# Revit family: xLIFE-xx-xx-SM_V1.0_Non-Hosted_R16
name_source: partatom
category: Lighting Fixtures
revit_build: Autodesk Revit 2016 (Build: 20151007_0715(x64)
units: mm (PartAtom-declared; Revit-internal decimal feet)

## family parameters
Always vertical = Yes
Cut with Voids When Loaded = No
Light Source = Yes
OmniClass Number = 23.80.70.00
OmniClass Title = Lighting
Part Type = Normal
Room Calculation Point = No
Round Connector Dimension = Use Diameter
Shared = No
Work Plane-Based = No

## types (27) — shared parameters
Charging Method = Intelligent Current Limited Constant Voltage
Color Filter = 16777215
Construction = Polycarbonate Enclosure
Dimensions (Lx W x H) = 242mm x 125mm x 48mm
Dimming Lamp Color Temperature Shift = <None>
Emit Shape Visible in Rendering = No
Emit from Rectangle Length = 1219 mm
Emit from Rectangle Width = 610 mm
IP Rating = IP20
Manufacturer = Clevertronics
Mounting = Surface Mount
Operating Mode = Non-maintained
Operating Temperature = 1˚C to 40˚C
Operating Voltage = 240V AC; 50Hz
Tilt Angle = 90.00°

## per-type parameters (varying)
| type | AS2293 Classification | Battery | Battery Type | Lamp | MIC Number | Photometric Web File | Power Consumption | Power Consumption (Standby) | Product Description | Replacement Battery | Replacement Driver | Testing Node | Testing System | Weight |
| ELIFE-X-LI-SM | C0=D40 C90=D40 | 3.2V 3200mAh | Lithium Iron Phosphate | 1 x High intensity LED | AUD03310010001 | ll22526_ELIFE-X-LI-SM(AUD03310010001,AS2293.3,Classification).ies | 1.3W (Max) | 0.4 W | Economy Lithium Lifelight, Surface Mounted Emergency Light | 1560160 BATT:EcoLith 3.2V 3.0Ah 170mm lead,NoBKT | 8002986 PCA: ELIFE-X-SMS-LI CT10614-L2 |  | N/A - Manual test switch | 0.6kg |
| LLIFE-SM-ZW | C0=D40 C90=D40 | 3.3V 2500mAh | Lithium Nanophosphate | 1 x High intensity LED | AUD01110050001 | LL22405 - CLIFE-SM-ZW (AUD02110010001, AS2293.3, 2-hr Photometry).ies | 2.7 Watts (Max) | 1.3 Watts | L10 Optimum Lifelight, High Performance, Surface Mounted Emergency Light | 1530071 BATTERY:L10 3.3V 2.5AH 200mm ld, no Brkt |  | 8001450 PCA:Powerline Node ZW, #CT10310-A6 | Zoneworks Computerised Testing | 0.6kg |
| LLIFE-SM-DALI | C0=D40 C90=D40 | 3.3V 2500mAh | Lithium Nanophosphate | 1 x High intensity LED | AUD01210070002 | LL22405 - CLIFE-SM-ZW (AUD02110010001, AS2293.3, 2-hr Photometry).ies | 2.7 Watts | 0.4 Watts | L10 Optimum Lifelight, High Performance, Surface Mounted Emergency Ligh | 1530071 BATTERY:L10 3.3V 2.5AH 200mm ld, no Brkt |  | 8003060 PCA: New DALI #CT10629-Ax | DALI Registered | 0.6kg |
| LLIFE-SM | C0=D40 C90=D40 | 3.3V 2500mAh | Lithium Nanophosphate | 1 x High intensity LED | AUD01310060001 | LL22405 - CLIFE-SM-ZW (AUD02110010001, AS2293.3, 2-hr Photometry).ies | 3.0 Watts | 1.3 Watts | L10 Optimum Lifelight, High Performance, Surface Mounted Emergency Light, Enabled
with Clevertest Plus | 1530071 BATTERY:L10 3.3V 2.5AH 200mm ld, no Brkt |  | 8002938 PCA: LLIFE CT10260-L5 1C550 CTP AU Vert Connectors | Clevertest Plus Enabled (Not activated by default) | 0.6kg |
| LLIFE-SM-BLK | C0=D40 C90=D40 | 3.3V 2.5AH | Lithium Iron Phosphate (LiFePO4), | 1 x LED | AUD01310070001 | LL22405 - CLIFE-SM-ZW (AUD02110010001, AS2293.3, 2-hr Photometry).ies | 4.2 Watts | 1.0 Watts | L10 Optimum LifeLight, High Performance, Recessed Emergency Light, Black, with Clevertest
L10 Optimum LifeLight, High Performance, Recessed Emergency Light, Black, with Clevertest
Plus Enabled


with Clevertest Plus | 1530071 BATTERY:L10 3.3V 2.5AH 200mm ld, no Brkt |  | 8002938 PCA: LLIFE CT10260-L5 1C550 CTP AU Vert Connectors | Clevertest Plus Enabled (Not activated by default) | 0.7kg |
| LLIFE-SM-HV | C0=D40 C90=D40 | 3.3V 2.5AH | Lithium Nanophosphate, | 1 x High intensity LED | AUD01810030001 | LL22405 - CLIFE-SM-ZW (AUD02110010001, AS2293.3, 2-hr Photometry).ies | 2.7 Watts | 0.4 Watts | L10 Optimum Lifelight, High Performance, Surface Mounted Emergency Light
L10 Optimum LifeLight, High Performance, Recessed Emergency Light, Black, with Clevertest
Plus Enabled


with Clevertest Plus | 1530071 BATTERY:L10 3.3V 2.5AH 200mm ld, no Brkt |  | 8003190 PCA: RF Node CT10678-Ax internal antenna | Zoneworks XT HIVE (RF) | 0.6kg |
| LLIFE-SM-HV-BLK | C0=D40 C90=D40 | 3.3V 2.5AH | Lithium Nanophosphate, | 1 x High intensity LED | AUD02810110001 | LL22405 - CLIFE-SM-ZW (AUD02110010001, AS2293.3, 2-hr Photometry).ies | 2.7 Watts | 1.3 Watts | L10 Optimum Lifelight, High Performance, Surface Mounted Emergency Light, Black
L10 Optimum LifeLight, High Performance, Recessed Emergency Light, Black, with Clevertest
Plus Enabled


with Clevertest Plus | 1530071 BATTERY:L10 3.3V 2.5AH 200mm ld, no Brkt |  | 8003190 PCA: RF Node CT10678-Ax internal antenna | Zoneworks XT HIVE (RF) | 0.6kg |
| CLIFE-SM-ZW | C0=D40 C90=D40 | 3.2V 3200mAh | Lithium Iron Phosphate | 1 x LED | AUD02110010001 | LL22405 - CLIFE-SM-ZW (AUD02110010001, AS2293.3, 2-hr Photometry).ies | 3.9 Watts | 1.0 W | LP Premium Lifelight, High Performance, Surface Mounted Emergency Light | 1550030 BATT:LP 3.2V 3200mAh 260mm lead,noBRKT |  | 8001450 PCA:Powerline Node ZW, #CT10310-A6 | Zoneworks computerised testing | 0.7kg |
| CLIFE-SM-ZW-BLK | C0=D40 C90=D40 | 3.2V 3200mAh | Lithium Iron Phosphate | 1 x LED | AUD02110060001 | LL22405 - CLIFE-SM-ZW (AUD02110010001, AS2293.3, 2-hr Photometry).ies | 3.9 Watts | 1.0 W | LP Premium Lifelight, High Performance, Surface Mounted Emergency Light, Black | 1550030 BATT:LP 3.2V 3200mAh 260mm lead,noBRKT |  | 8001450 PCA:Powerline Node ZW, #CT10310-A6 | Zoneworks computerised testing | 0.7kg |
| CLIFE-SM-DALI | C0=D40 C90=D40 | 3.2V 3200mAh | Lithium Iron Phosphate | 1 x LED | AUD02210200002 | LL22405 - CLIFE-SM-ZW (AUD02110010001, AS2293.3, 2-hr Photometry).ies | 3.9 Watts | 1.0 W | LP Premium Lifelight, High Performance, Surface Mounted Emergency Light | 1550030 BATT:LP 3.2V 3200mAh 260mm lead,noBRKT |  | 8003060 PCA: DALI Node #CT10629-Ax | DALI Registered | 0.7kg |
| CLIFE-SM | C0=D40 C90=D40 | 3.2V 3200mAh | Lithium Iron Phosphate | 1 x LED | AUD02310030001 | LL22405 - CLIFE-SM-ZW (AUD02110010001, AS2293.3, 2-hr Photometry).ies | 3.9 Watts | 1.0 W | LP Premium Lifelight, High Performance, Surface Mounted Emergency Light, Enabled with
Clevertest Plus | 1550030 BATT:LP 3.2V 3200mAh 260mm lead,noBRKT |  | 8002934 PCA: CLIFE CT10260-L5 1C650 CTP AU Vert Connectors | Clevertest Plus Enabled (Not activated by default) | 0.7kg |
| CLIFE-SM-4HR | C0=D40 C90=D40 | 3.2V 6400mAh | Lithium Iron Phosphate | 1 x High intensity LED | AUD02310080001 | LL22405 - CLIFE-SM-ZW (AUD02110010001, AS2293.3, 2-hr Photometry).ies | 3.9 Watts | 1.0 W | LP Premium Lifelight, High Performance, Surface Mounted Emergency Light with 4 Hour
Emergency Operation
Clevertest Plus | 1550231 BATT:LP 3.2V 6400mAh.200mm lead, No Brkt |  | 8002934 PCA: CLIFE CT10260-L5 1C650 CTP AU Vert Connectors | Manual (see datasheet) | 0.7kg |
| CLIFE-SM-HV | C0=D40 C90=D40 | 3.2V 3200mAh | Lithium Iron Phosphate | 1 x High intensity LED | AUD02810080001 | LL22405 - CLIFE-SM-ZW (AUD02110010001, AS2293.3, 2-hr Photometry).ies | 3.9 Watts | 1.0 W | LP Premium Lifelight, High Performance, Surface Mounted Emergency Light | 1550030 BATT:LP 3.2V 3200mAh 260mm lead,noBRKT. |  | 8003190 PCA: RF Node CT10678-Ax Int Antenna | Zoneworks XT HIVE (RF) | 0.7kg |
| CLIFE-SM-BLK | C0=D40 C90=D40 | 3.2V 3200mAh | Lithium Iron Phosphate | 1 x High intensity LED | AUD02810090001 | LL22405 - CLIFE-SM-ZW (AUD02110010001, AS2293.3, 2-hr Photometry).ies | 3.9 Watts | 1.0 W | LP Premium Lifelight, High Performance, Surface Mounted Emergency Light, Black,
Enabled with Clevertest Plus | 1550030 BATT:LP 3.2V 3200mAh 260mm lead,noBRKT. |  | 8002934 PCA: CLIFE CT10260-L5 1C650 CTP AU Vert Connectors | Clevertest Plus Enabled (Not activated by default) | 0.7kg |
| CLIFE-SM-HV-BLK | C0=D40 C90=D40 | 3.2V 3200mAh | Lithium Iron Phosphate | 1 x High intensity LED | AUD02810100001 | LL22405 - CLIFE-SM-ZW (AUD02110010001, AS2293.3, 2-hr Photometry).ies | 3.9 Watts | 1.0 W | LP Premium Lifelight, High Performance, Surface Mounted Emergency Light, Black
Enabled with Clevertest Plus | 1550030 BATT:LP 3.2V 3200mAh 260mm lead,noBRKT. |  | 8003190 PCA: RF Node CT10678-Ax Int Antenna | Zoneworks XT HIVE (RF) | 0.7kg |
| LLIFE-PRO-SM-DALI | C0=D80 C90=D80 | 3.3V 5000mAh | Lithium Nanophosphate | Dual LED | AUT01210570002 | ll22440(AS2293.3_Photometry).ies | 4.7 Watts | 0.4W | L10 Optimum Lifelight PRO, High Performance, Surface Mounted Emergency Light
Enabled with Clevertest Plus | 1530231 BATTERY:L10 3.3V 5AH. 200mm lead.no Brkt |  | 8003060 PCA: New DALI #CT10629-Ax | DALI Registered | 0.7kg |
| LLIFE-PRO-SM | C0=D80 C90=D80 | 3.3V 5000mAh | Lithium Nanophosphate | Dual LED | AUT01310080001 | ll22440(AS2293.3_Photometry).ies | 4.7 Watts | 0.4W | L10 Optimum Lifelight PRO, High Performance, Surface Mounted Emergency Light,
Enabled with Clevertest Plus
Enabled with Clevertest Plus | 1530231 BATTERY:L10 3.3V 5AH. 200mm lead.no Brkt |  | 8002924 PCA: xLIFEPro SM #CT10142-L9 2C250/550 CTP AU | Clevertest Plus Enabled (Not activated by default) | 0.7kg |
| LLIFE-PRO-SM-BLK | C0=D80 C90=D80 | 3.3V 5000mAh | Lithium Nanophosphate | Dual LED | AUT01310110001 | ll22440(AS2293.3_Photometry).ies | 4.7 Watts | 0.4W | L10 Optimum Lifelight PRO, High Performance, Surface Mounted Emergency Light,
Enabled with Clevertest Plus, Black
Enabled with Clevertest Plus
Enabled with Clevertest Plus | 1530231 BATTERY:L10 3.3V 5AH. 200mm lead.no Brkt |  | 8002924 PCA: xLIFEPro SM #CT10142-L9 2C250/550 CTP AU | Clevertest Plus Enabled (Not activated by default) | 0.7kg |
| LLIFE-PRO-SM-HV | C0=D80 C90=D80 | 3.3V 5000mAh | Lithium Nanophosphate | Dual LED | AUT01810030001 | ll22440(AS2293.3_Photometry).ies | 4.7 Watts | 0.4W | L10 Optimum Lifelight PRO, High Performance, Surface Mounted Emergency Light
Enabled with Clevertest Plus, Black
Enabled with Clevertest Plus
Enabled with Clevertest Plus | 1530231 BATTERY:L10 3.3V 5AH. 200mm lead.no Brkt |  | 8003191 PCA: RF Node CT10678-A9 Int Antenna LLPro | Zoneworks XT Hive (RF) | 0.7kg |
| LLIFE-PRO-SM-HV-BLK | C0=D80 C90=D80 | 3.3V 5000mAh | Lithium Nanophosphate | Dual LED | AUT02810070001 | ll22440(AS2293.3_Photometry).ies | 4.7 Watts | 0.4W | L10 Optimum Lifelight PRO, High Performance, Surface Mounted Emergency Light, Black
Enabled with Clevertest Plus, Black
Enabled with Clevertest Plus
Enabled with Clevertest Plus | 1530231 BATTERY:L10 3.3V 5AH. 200mm lead.no Brkt |  | 8003191 PCA: RF Node CT10678-A9 Int Antenna LLPro | Zoneworks XT Hive (RF) | 0.7kg |
| CLIFE-PRO-SM-ZW | C0=D80 C90=D80 | 3.2V 6400mAh | Lithium Iron Phosphate | Dual LED | AUT02110060001 | ll22440(AS2293.3_Photometry).ies | 2.7W Watts | 0.4W | LP Premium Lifelight PRO, High Performance, Surface Mounted Emergency Light
Enabled with Clevertest Plus, Black
Enabled with Clevertest Plus
Enabled with Clevertest Plus | 1550231 BATT:LP 3.2V 6400mAh.200mm lead, No Brkt |  | 8001450 PCA:Powerline Node ZW, #CT10310-A6 | Zoneworks Computerised Testing | 0.7kg |
| CLIFE-PRO-SM-ZW-BLK | C0=D80 C90=D80 | 3.2V 6400mAh | Lithium Iron Phosphate | Dual LED | AUT02110130001 | ll22440(AS2293.3_Photometry).ies | 2.7W Watts | 0.4W | LP Premium Lifelight PRO, High Performance, Surface Mounted Emergency Light
Enabled with Clevertest Plus, Black
Enabled with Clevertest Plus
LP Premium Lifelight PRO, High Performance, Surface Mounted Emergency Light, Black | 1550231 BATT:LP 3.2V 6400mAh.200mm lead, No Brkt |  | 8001450 PCA:Powerline Node ZW, #CT10310-A6 | Zoneworks Computerised Testing | 0.7kg |
| CLIFE-PRO-SM-DALI | C0=D80 C90=D80 | 3.2V 6400mAh | Lithium Iron Phosphate | Dual LED | AUT02210330002 | ll22440(AS2293.3_Photometry).ies | 2.7W Watts | 0.4W | LP Premium Lifelight PRO, High Performance, Surface Mounted Emergency Light
Enabled with Clevertest Plus, Black
Enabled with Clevertest Plus
LP Premium Lifelight PRO, High Performance, Surface Mounted Emergency Light, Black | 1550231 BATT:LP 3.2V 6400mAh.200mm lead, No Brkt |  | 8003060 PCA: New DALI #CT10629-Ax | DALI Registered | 0.7kg |
| CLIFE-PRO-SM | C0=D80 C90=D80 | 3.2V 6400mAh | Lithium Iron Phosphate | Dual LED | AUT02310110001 | ll22440(AS2293.3_Photometry).ies | 4.7W | 0.4W | LP Premium Lifelight PRO, High Performance, Surface Mounted Emergency Light,
Enabled with Clevertest Plus
Enabled with Clevertest Plus, Black
Enabled with Clevertest Plus
LP Premium Lifelight PRO, High Performance, Surface Mounted Emergency Light, Black | 1550231 BATT:LP 3.2V 6400mAh.200mm lead, No Brkt |  | 8002924 PCA: xLIFEPro SM #CT10142-L9 2C250/550 CTP AU | Clevertest Plus Enabled (Not activated by default) | 0.7kg |
| CLIFE-PRO-SM-BLK | C0=D80 C90=D80 | 3.2V 6400mAh | Lithium Iron Phosphate | Dual LED | AUT02310170001 | ll22440(AS2293.3_Photometry).ies | 2.7W Watts | 0.4W | LP Premium Lifelight PRO, High Performance, Surface Mounted Emergency Light,
Enabled with Clevertest Plus, Black
Enabled with Clevertest Plus, Black
Enabled with Clevertest Plus
LP Premium Lifelight PRO, High Performance, Surface Mounted Emergency Light, Black | 1550231 BATT:LP 3.2V 6400mAh.200mm lead, No Brkt |  | 8002924 PCA: xLIFEPro SM #CT10142-L9 2C250/550 CTP AU | Clevertest Plus Enabled (Not activated by default) | 0.7kg |
| CLIFE-PRO-SM-HV | C0=D80 C90=D80 | 3.2V 6400mAh | Lithium Iron Phosphate | Dual LED | AUT02810050001 | ll22440(AS2293.3_Photometry).ies | 2.7W Watts | 0.4W | LP Premium Lifelight PRO, High Performance, Surface Mounted Emergency Light
Enabled with Clevertest Plus, Black
Enabled with Clevertest Plus, Black
Enabled with Clevertest Plus
LP Premium Lifelight PRO, High Performance, Surface Mounted Emergency Light, Black | 1550231 BATT:LP 3.2V 6400mAh.200mm lead, No Brkt |  | 8003191 PCA: RF Node CT10678-A9 Int Antenna LLPro | Zoneworks XT HIVE (RF) | 0.7kg |
| CLIFE-PRO-SM-HV-BLK | C0=D80 C90=D80 | 3.2V 6400mAh | Lithium Iron Phosphate | Dual LED | AUT02810060001 | ll22440(AS2293.3_Photometry).ies | 2.7W Watts | 0.4W | LP Premium Lifelight PRO, High Performance, Surface Mounted Emergency Light,
Black
Enabled with Clevertest Plus, Black
Enabled with Clevertest Plus, Black
Enabled with Clevertest Plus
LP Premium Lifelight PRO, High Performance, Surface Mounted Emergency Light, Black | 1550231 BATT:LP 3.2V 6400mAh.200mm lead, No Brkt |  | 8003191 PCA: RF Node CT10678-A9 Int Antenna LLPro | Zoneworks XT HIVE (RF) | 0.7kg |

note: column(s) folded — value = type name in every type: Model

## geometry (parser evidence)
native form markers: Sweep x2
no freeform markers — native parametric forms only
